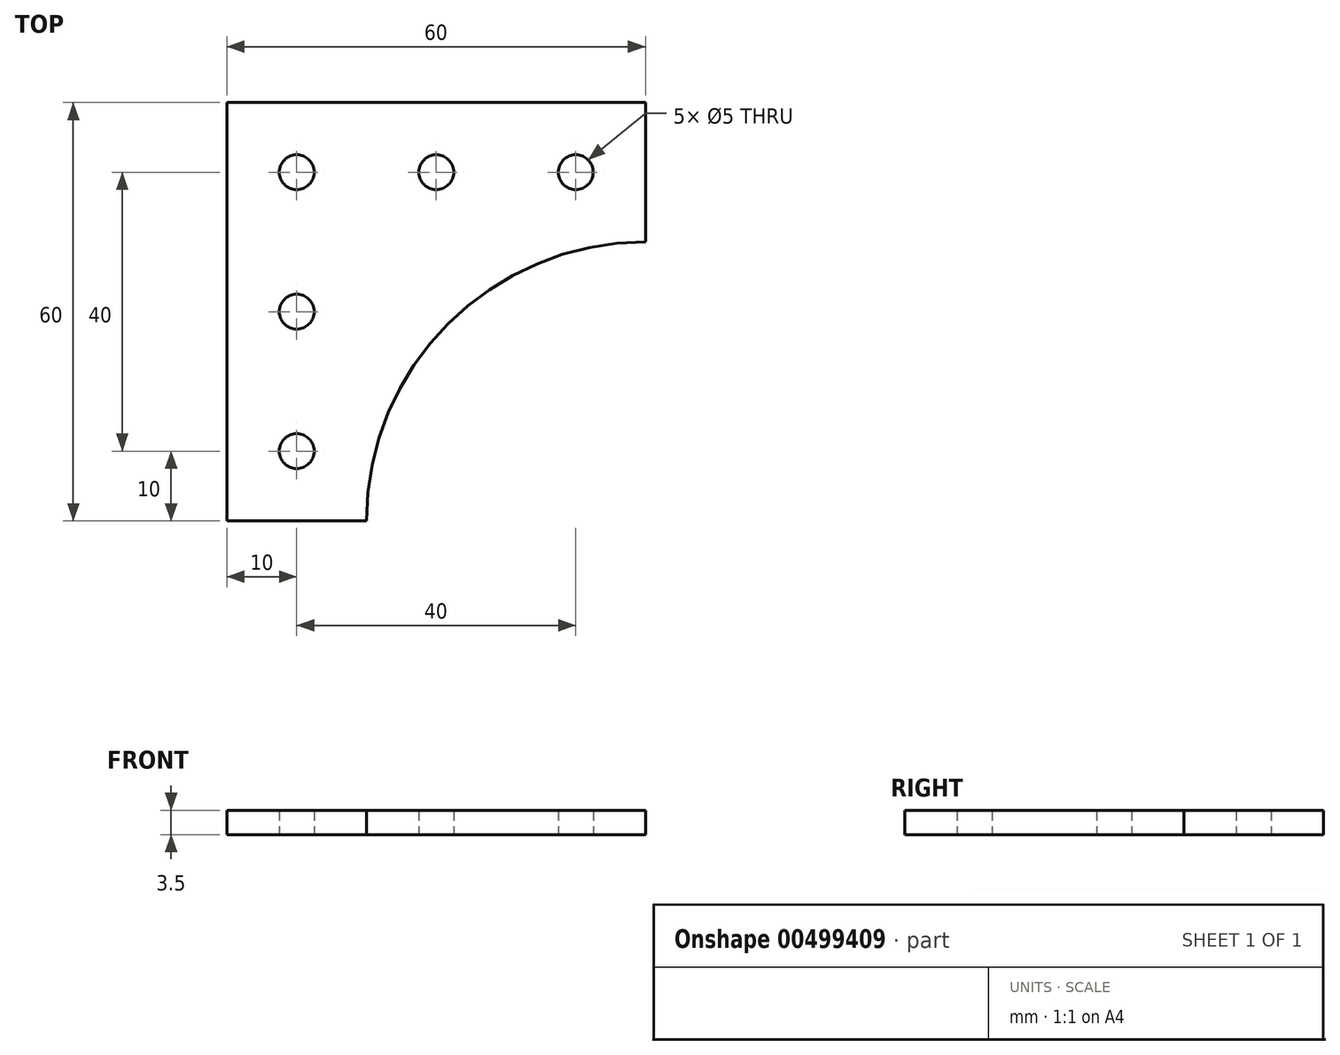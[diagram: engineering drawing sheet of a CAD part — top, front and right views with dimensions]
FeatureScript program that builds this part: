
annotation { "Feature Type Name" : "Feature", "Feature Type Description" : "" }
export const myFeature = defineFeature(function(context is Context, id is Id, definition is map)
    precondition{}
    {
        {
            var Q0;
            Q0=qCreatedBy(makeId("Top.planeOp"),FACE);
            var sketch = newSketch(context, id + "F0", { "sketchPlane" : qUnion([Q0])});
            skLineSegment(sketch, "E0.bottom", {"start": v(-30, -30) * mm, "end": v(30, -30) * mm});
            skLineSegment(sketch, "E0.top", {"start": v(-30, 30) * mm, "end": v(30, 30) * mm});
            skLineSegment(sketch, "E0.left", {"start": v(-30, -30) * mm, "end": v(-30, 30) * mm});
            skLineSegment(sketch, "E0.right", {"start": v(30, -30) * mm, "end": v(30, 30) * mm});
            skPoint(sketch, "E0.middle", {"position": v(0, 0) * mm});
            skLineSegment(sketch, "E1", {"start": v(-10, 30) * mm, "end": v(-10, -30) * mm, "construction": true});
            skLineSegment(sketch, "E2", {"start": v(-30, 10) * mm, "end": v(30, 10) * mm, "construction": true});
            skArc(sketch, "E3", {"start": v(30, 10) * mm, "mid": v(1.72, -1.72) * mm, "end": v(-10, -30) * mm});
            skPoint(sketch, "E4", {"position": v(-30, 20) * mm});
            skPoint(sketch, "E5", {"position": v(-20, 30) * mm});
            skCircle(sketch, "E6", {"center": v(-20, 20) * mm, "radius": 2.5 * mm});
            skPoint(sketch, "E7", {"position": v(-30, 0) * mm});
            skPoint(sketch, "E8", {"position": v(-30, -20) * mm});
            skCircle(sketch, "E9", {"center": v(-20, 0) * mm, "radius": 2.5 * mm});
            skCircle(sketch, "E10", {"center": v(-20, -20) * mm, "radius": 2.5 * mm});
            skPoint(sketch, "E11", {"position": v(0, 30) * mm});
            skPoint(sketch, "E12", {"position": v(20, 30) * mm});
            skCircle(sketch, "E13", {"center": v(0, 20) * mm, "radius": 2.5 * mm});
            skCircle(sketch, "E14", {"center": v(20, 20) * mm, "radius": 2.5 * mm});
            skSolve(sketch);
        }
        {
            var Q0;
            {var subQ1=sQuery(id+"F0.wireOp",EDGE,"E0.top");Q0=makeQuery(id+"F0.imprint","IMPRINT",FACE,{"disambiguationData":[TD([[makeQuery(id+"F0.imprint","IMPRINT",EDGE,{"derivedFrom":subQ1}),-1.0]])]});}
            extrude(context, id + "F1", {"entities" : qUnion([Q0]), "depth" : 3.5 * mm, "offsetDistance" : 25 * mm});
        }
    });
